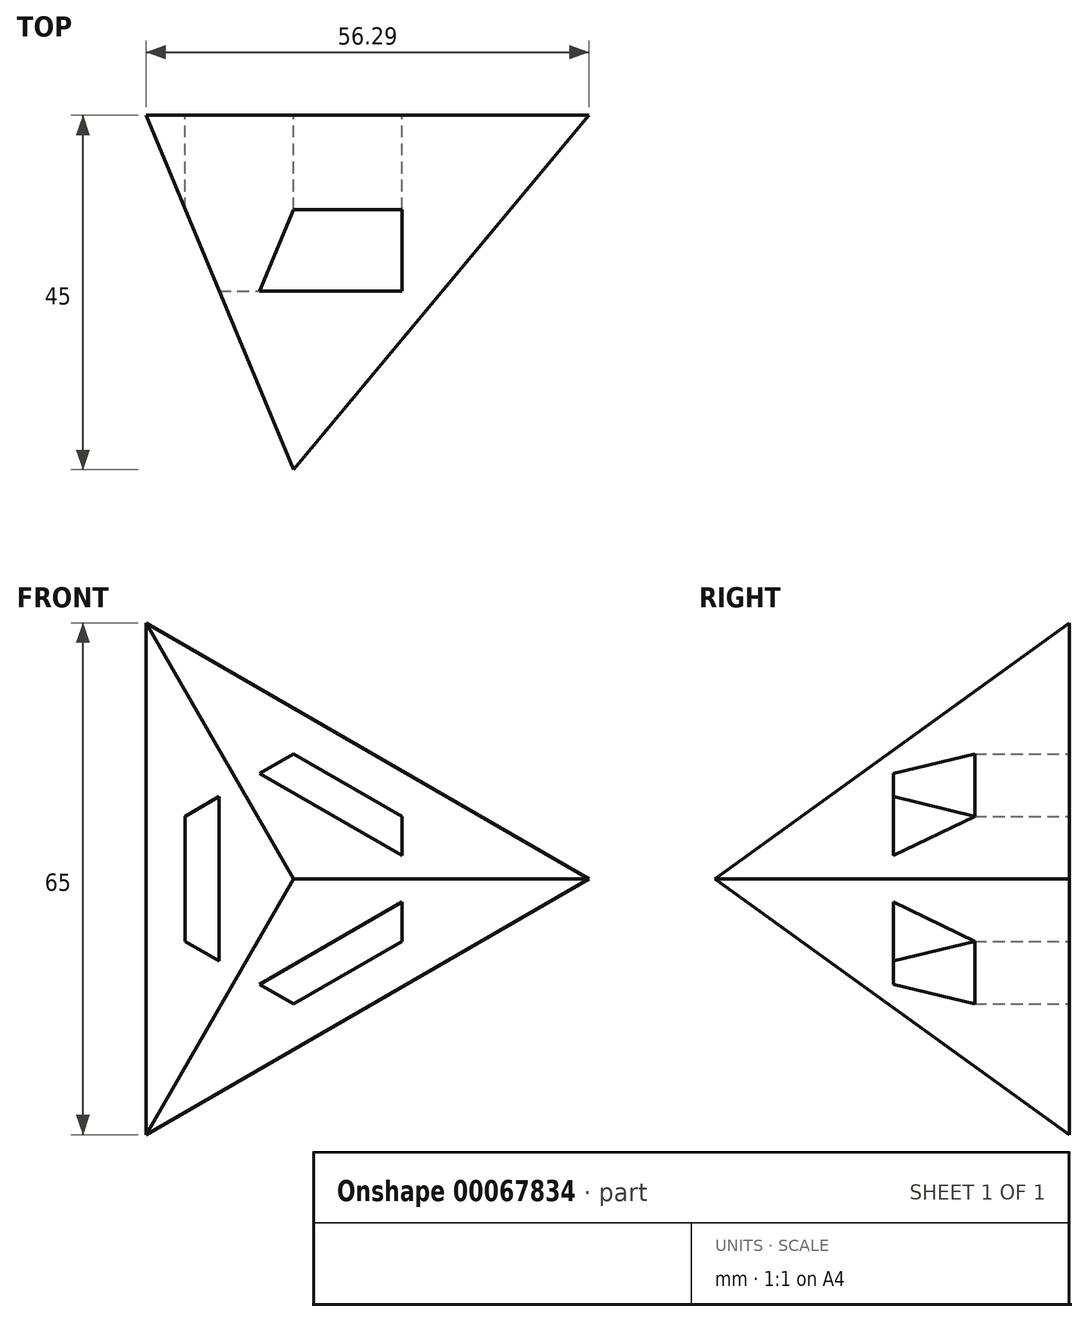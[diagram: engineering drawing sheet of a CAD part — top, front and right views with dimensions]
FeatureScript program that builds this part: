
annotation { "Feature Type Name" : "Feature", "Feature Type Description" : "" }
export const myFeature = defineFeature(function(context is Context, id is Id, definition is map)
    precondition{}
    {
        {
            var Q0;
            Q0=qCreatedBy(makeId("Front.planeOp"),FACE);
            var sketch = newSketch(context, id + "F0", { "sketchPlane" : qUnion([Q0])});
            skCircle(sketch, "E0.cCircle", {"center": v(0, 0) * mm, "radius": 18.76 * mm, "construction": true});
            skLineSegment(sketch, "E0.0", {"start": v(-18.76, 32.5) * mm, "end": v(37.53, 0) * mm});
            skLineSegment(sketch, "E0.1", {"start": v(37.53, 0) * mm, "end": v(-18.76, -32.5) * mm});
            skLineSegment(sketch, "E0.2", {"start": v(-18.76, -32.5) * mm, "end": v(-18.76, 32.5) * mm});
            skPoint(sketch, "E0.0.midPoint", {"position": v(9.38, 16.25) * mm});
            skSolve(sketch);
        }
        {
            var Q0;
            Q0=makeQuery(id+"F0.imprint","IMPRINT",FACE,{"disambiguationData":[TD([[makeQuery(id+"F0.imprint","IMPRINT",EDGE,{"derivedFrom":sQuery(id+"F0.wireOp",EDGE,"E0.0")}),-1.0]])]});
            cPlane(context, id + "F1", {"entities" : qUnion([Q0]), "cplaneType" : CPlaneType.OFFSET, "offset" : 45 * mm, "width" : 150 * mm, "height" : 150 * mm});
        }
        {
            var Q0;
            Q0=qCreatedBy(id+"F1.planeOp",FACE);
            var sketch = newSketch(context, id + "F2", { "sketchPlane" : qUnion([Q0])});
            skPoint(sketch, "E1", {"position": v(0, 0) * mm});
            skSolve(sketch);
        }
        {
            var Q0;
            Q0=makeQuery(id+"F0.imprint","IMPRINT",FACE,{"disambiguationData":[TD([[makeQuery(id+"F0.imprint","IMPRINT",EDGE,{"derivedFrom":sQuery(id+"F0.wireOp",EDGE,"E0.0")}),-1.0]])]});
            var Q1;
            Q1=sQuery(id+"F2.wireOp",VERTEX,"E1");
            loft(context, id + "F3", {"sheetProfilesArray" : [{ "sheetProfileEntities" : qUnion([Q0]) }, { "sheetProfileEntities" : qUnion([Q1]) }]});
        }
        {
            var Q0;
            {var subQ0=sQuery(id+"F0.wireOp",EDGE,"E0.1");var subQ1=sQuery(id+"F0.wireOp",EDGE,"E0.2");var subQ2=sQuery(id+"F0.wireOp",EDGE,"E0.0");Q0=makeQuery(id+"F3.opLoft","SWEPT_FACE",FACE,{"disambiguationData":[OSD([subQ2,subQ0,subQ1]),TDD([makeQuery(id+"F0.imprint","INTERSECT",VERTEX,{"derivedFrom":[subQ2,subQ0]}),makeQuery(id+"F0.imprint","INTERSECT",VERTEX,{"derivedFrom":[subQ0,subQ1]}),makeQuery(id+"F0.imprint","IMPRINT",EDGE,{"derivedFrom":subQ0})])]});}
            var sketch = newSketch(context, id + "F4", { "sketchPlane" : qUnion([Q0])});
            skSolve(sketch);
        }
        {
            var Q0;
            Q0=makeQuery(id+"F3.opLoft","CAP_FACE",FACE,{"disambiguationData":[OSD([makeQuery(id+"F0.imprint","IMPRINT",FACE,{"disambiguationData":[TD([[makeQuery(id+"F0.imprint","IMPRINT",EDGE,{"derivedFrom":sQuery(id+"F0.wireOp",EDGE,"E0.0")}),-1.0]])]})])],"isStart":true});
            var sketch = newSketch(context, id + "F5", { "sketchPlane" : qUnion([Q0])});
            skCircle(sketch, "E2.cCircle", {"center": v(0, 0) * mm, "radius": 13.76 * mm, "construction": true});
            skLineSegment(sketch, "E2.0", {"start": v(0, -15.9) * mm, "end": v(-13.76, -7.95) * mm});
            skLineSegment(sketch, "E2.1", {"start": v(-13.76, -7.95) * mm, "end": v(-13.76, 7.95) * mm});
            skLineSegment(sketch, "E2.2", {"start": v(-13.76, 7.95) * mm, "end": v(0, 15.9) * mm});
            skLineSegment(sketch, "E2.3", {"start": v(0, 15.9) * mm, "end": v(13.76, 7.95) * mm});
            skLineSegment(sketch, "E2.4", {"start": v(13.76, 7.95) * mm, "end": v(13.76, -7.95) * mm});
            skLineSegment(sketch, "E2.5", {"start": v(13.76, -7.95) * mm, "end": v(0, -15.9) * mm});
            skPoint(sketch, "E2.0.midPoint", {"position": v(-6.88, -11.92) * mm});
            skSolve(sketch);
        }
        {
            var Q0;
            Q0=makeQuery(id+"F5.imprint","IMPRINT",FACE,{"disambiguationData":[TD([[makeQuery(id+"F5.imprint","IMPRINT",EDGE,{"derivedFrom":sQuery(id+"F5.wireOp",EDGE,"E2.0")}),-1.0]])]});
            extrude(context, id + "F6", {"entities" : qUnion([Q0]), "operationType" : NewBodyOperationType.REMOVE, "oppositeDirection" : true, "depth" : 22.35 * mm});
        }
    });
